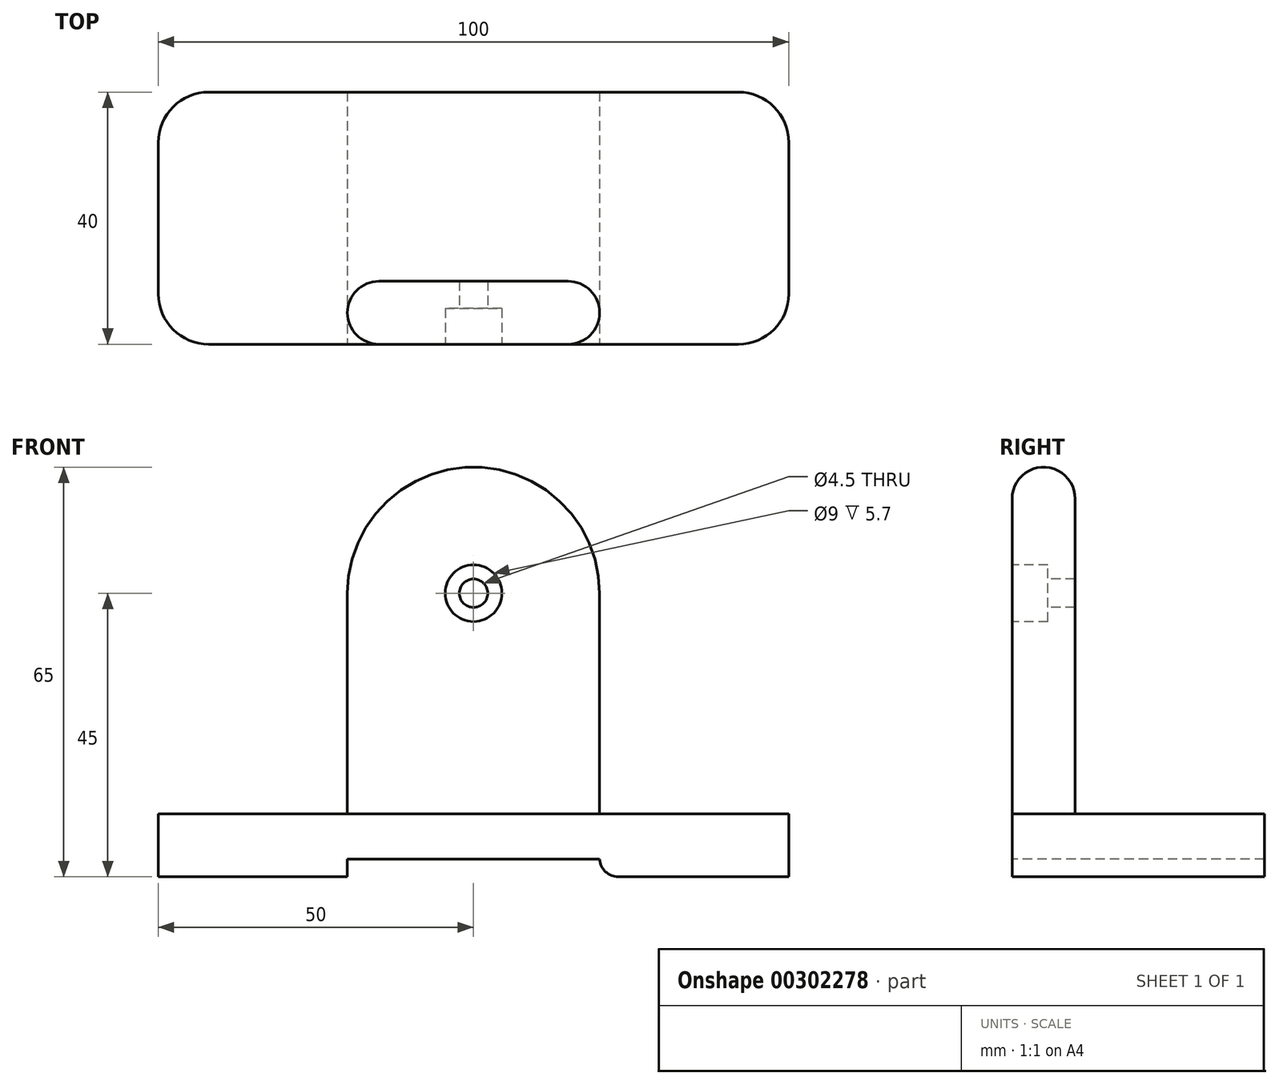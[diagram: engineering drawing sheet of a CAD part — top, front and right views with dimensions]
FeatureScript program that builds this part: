
annotation { "Feature Type Name" : "Feature", "Feature Type Description" : "" }
export const myFeature = defineFeature(function(context is Context, id is Id, definition is map)
    precondition{}
    {
        {
            var Q0;
            Q0=qCreatedBy(makeId("Top.planeOp"),FACE);
            var sketch = newSketch(context, id + "F0", { "sketchPlane" : qUnion([Q0])});
            skLineSegment(sketch, "E0.bottom", {"start": v(-100, 40) * mm, "end": v(0, 40) * mm});
            skLineSegment(sketch, "E0.top", {"start": v(-100, 0) * mm, "end": v(0, 0) * mm});
            skLineSegment(sketch, "E0.left", {"start": v(-100, 40) * mm, "end": v(-100, 0) * mm});
            skLineSegment(sketch, "E0.right", {"start": v(0, 40) * mm, "end": v(0, 0) * mm});
            skSolve(sketch);
        }
        {
            var Q0;
            Q0 = qSketchRegion(id + "F0", true);
            extrude(context, id + "F1", {"entities" : qUnion([Q0]), "depth" : 10 * mm});
        }
        {
            var Q0;
            Q0=makeQuery(id+"F1.opExtrude","SWEPT_FACE",FACE,{"disambiguationData":[OSD([sQuery(id+"F0.wireOp",EDGE,"E0.top")])]});
            var sketch = newSketch(context, id + "F2", { "sketchPlane" : qUnion([Q0])});
            skLineSegment(sketch, "E1", {"start": v(-70, 10) * mm, "end": v(-30, 10) * mm});
            skLineSegment(sketch, "E2", {"start": v(-70, 45) * mm, "end": v(-70, 10) * mm});
            skLineSegment(sketch, "E3", {"start": v(-30, 45) * mm, "end": v(-30, 10) * mm});
            skArc(sketch, "E4", {"start": v(-70, 45) * mm, "mid": v(-50, 65) * mm, "end": v(-30, 45) * mm});
            skSolve(sketch);
        }
        {
            var Q0;
            Q0 = qSketchRegion(id + "F2", true);
            extrude(context, id + "F3", {"entities" : qUnion([Q0]), "oppositeDirection" : true, "depth" : 10 * mm});
        }
        {
            var Q0;
            Q0=makeQuery(id+"F1.opExtrude","SWEPT_FACE",FACE,{"disambiguationData":[OSD([sQuery(id+"F0.wireOp",EDGE,"E0.top")])]});
            var sketch = newSketch(context, id + "F4", { "sketchPlane" : qUnion([Q0])});
            skLineSegment(sketch, "E5.bottom", {"start": v(-70, 0) * mm, "end": v(-30, 0) * mm});
            skLineSegment(sketch, "E5.top", {"start": v(-70, 2.79) * mm, "end": v(-30, 2.79) * mm});
            skLineSegment(sketch, "E5.left", {"start": v(-70, 0) * mm, "end": v(-70, 2.79) * mm});
            skLineSegment(sketch, "E5.right", {"start": v(-30, 0) * mm, "end": v(-30, 2.79) * mm});
            skSolve(sketch);
        }
        {
            var Q0;
            Q0 = qSketchRegion(id + "F4", true);
            extrude(context, id + "F5", {"entities" : qUnion([Q0]), "operationType" : NewBodyOperationType.REMOVE, "endBound" : BoundingType.THROUGH_ALL, "oppositeDirection" : true, "depth" : 25 * mm});
        }
        {
            var Q0;
            Q0=makeQuery(id+"F3.opExtrude","CAP_FACE",FACE,{"disambiguationData":[OSD([sQuery(id+"F2.wireOp",EDGE,"E1"),sQuery(id+"F2.wireOp",EDGE,"E2"),sQuery(id+"F2.wireOp",EDGE,"E3"),sQuery(id+"F2.wireOp",EDGE,"E4")])],"isStart":true});
            var sketch = newSketch(context, id + "F6", { "sketchPlane" : qUnion([Q0])});
            skCircle(sketch, "E6", {"center": v(-50, 45) * mm, "radius": 2.25 * mm});
            skSolve(sketch);
        }
        {
            var Q0;
            Q0 = qSketchRegion(id + "F6", true);
            extrude(context, id + "F7", {"entities" : qUnion([Q0]), "operationType" : NewBodyOperationType.REMOVE, "endBound" : BoundingType.THROUGH_ALL, "oppositeDirection" : true, "depth" : 25 * mm});
        }
        {
            var Q0;
            Q0=makeQuery(id+"F3.opExtrude","CAP_FACE",FACE,{"disambiguationData":[OSD([sQuery(id+"F2.wireOp",EDGE,"E1"),sQuery(id+"F2.wireOp",EDGE,"E2"),sQuery(id+"F2.wireOp",EDGE,"E3"),sQuery(id+"F2.wireOp",EDGE,"E4")])],"isStart":true});
            var sketch = newSketch(context, id + "F8", { "sketchPlane" : qUnion([Q0])});
            skCircle(sketch, "E7", {"center": v(-50, 45) * mm, "radius": 4.5 * mm});
            skSolve(sketch);
        }
        {
            var Q0;
            Q0 = qSketchRegion(id + "F8", true);
            extrude(context, id + "F9", {"entities" : qUnion([Q0]), "operationType" : NewBodyOperationType.REMOVE, "oppositeDirection" : true, "depth" : 5.7 * mm});
        }
        {
            var Q0;
            Q0=makeQuery(id+"F1.opExtrude","SWEPT_EDGE",EDGE,{"disambiguationData":[OSD([sQuery(id+"F0.wireOp",EDGE,"E0.top"),sQuery(id+"F0.wireOp",EDGE,"E0.left")])]});
            var Q1;
            Q1=makeQuery(id+"F1.opExtrude","SWEPT_EDGE",EDGE,{"disambiguationData":[OSD([sQuery(id+"F0.wireOp",EDGE,"E0.bottom"),sQuery(id+"F0.wireOp",EDGE,"E0.left")])]});
            var Q2;
            Q2=makeQuery(id+"F1.opExtrude","SWEPT_EDGE",EDGE,{"disambiguationData":[OSD([sQuery(id+"F0.wireOp",EDGE,"E0.top"),sQuery(id+"F0.wireOp",EDGE,"E0.right")])]});
            var Q3;
            Q3=makeQuery(id+"F1.opExtrude","SWEPT_EDGE",EDGE,{"disambiguationData":[OSD([sQuery(id+"F0.wireOp",EDGE,"E0.bottom"),sQuery(id+"F0.wireOp",EDGE,"E0.right")])]});
            fillet(context, id + "F10", {"entities" : qUnion([Q0, Q1, Q2, Q3]), "radius" : 8 * mm, "tangentPropagation" : true, "allowEdgeOverflow" : false});
        }
        {
            var Q0;
            Q0=makeQuery(id+"F5.boolean.opBoolean","COPY",EDGE,{"derivedFrom":makeQuery(id+"F5.opExtrude","SWEPT_EDGE",EDGE,{"disambiguationData":[OSD([sQuery(id+"F0.wireOp",EDGE,"E0.top"),sQuery(id+"F4.wireOp",EDGE,"E5.bottom"),sQuery(id+"F4.wireOp",EDGE,"E5.left")])]})});
            var Q1;
            Q1=makeQuery(id+"F5.boolean.opBoolean","COPY",EDGE,{"derivedFrom":makeQuery(id+"F5.opExtrude","SWEPT_EDGE",EDGE,{"disambiguationData":[OSD([sQuery(id+"F0.wireOp",EDGE,"E0.top"),sQuery(id+"F4.wireOp",EDGE,"E5.bottom"),sQuery(id+"F4.wireOp",EDGE,"E5.right")])]})});
            var Q2;
            Q2=makeQuery(id+"F9.boolean.opBoolean","COPY",EDGE,{"derivedFrom":makeQuery(id+"F9.opExtrude","CAP_EDGE",EDGE,{"disambiguationData":[OSD([sQuery(id+"F8.wireOp",EDGE,"E7")])],"isStart":true})});
            fillet(context, id + "F11", {"entities" : qUnion([Q0, Q1, Q2]), "radius" : 3 * mm, "tangentPropagation" : true, "allowEdgeOverflow" : false});
        }
        {
            var Q0;
            Q0=makeQuery(id+"F3.opExtrude","CAP_EDGE",EDGE,{"disambiguationData":[OSD([sQuery(id+"F2.wireOp",EDGE,"E3")])],"isStart":true});
            var Q1;
            Q1=makeQuery(id+"F3.opExtrude","CAP_EDGE",EDGE,{"disambiguationData":[OSD([sQuery(id+"F2.wireOp",EDGE,"E3")])],"isStart":false});
            fillet(context, id + "F12", {"entities" : qUnion([Q0, Q1]), "radius" : 5 * mm, "tangentPropagation" : true, "allowEdgeOverflow" : false});
        }
    });
